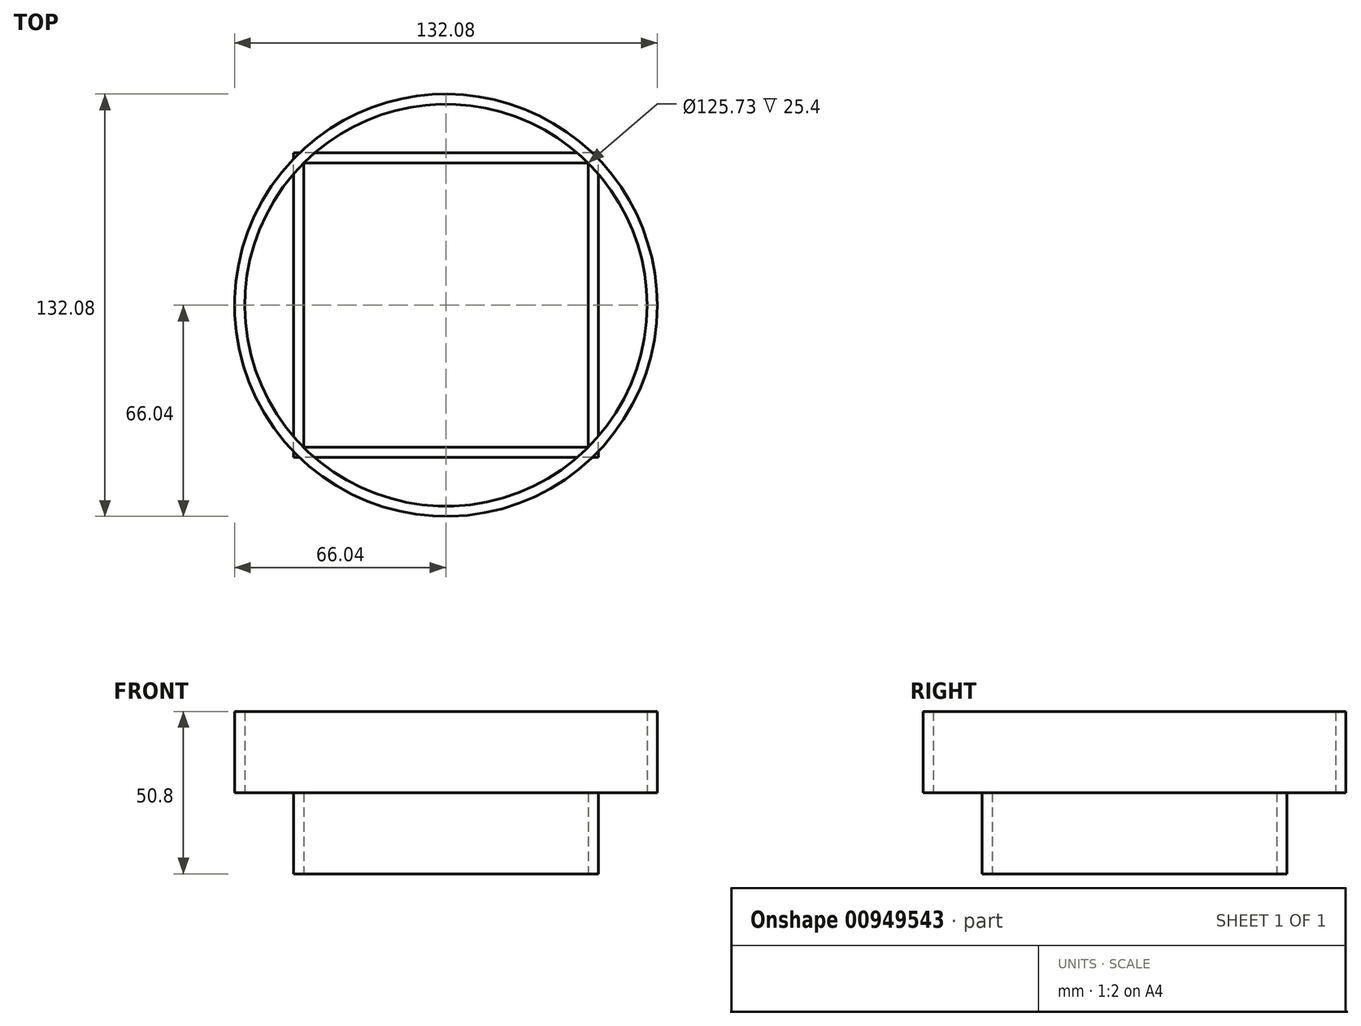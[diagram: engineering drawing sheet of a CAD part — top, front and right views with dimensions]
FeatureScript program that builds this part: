
annotation { "Feature Type Name" : "Feature", "Feature Type Description" : "" }
export const myFeature = defineFeature(function(context is Context, id is Id, definition is map)
    precondition{}
    {
        {
            var Q0;
            Q0=qCreatedBy(makeId("Top.planeOp"),FACE);
            var sketch = newSketch(context, id + "F0", { "sketchPlane" : qUnion([Q0])});
            skLineSegment(sketch, "E0.bottom", {"start": v(44.45, -44.45) * mm, "end": v(-44.45, -44.45) * mm});
            skLineSegment(sketch, "E0.top", {"start": v(44.45, 44.45) * mm, "end": v(-44.45, 44.45) * mm});
            skLineSegment(sketch, "E0.left", {"start": v(44.45, -44.45) * mm, "end": v(44.45, 44.45) * mm});
            skLineSegment(sketch, "E0.right", {"start": v(-44.45, -44.45) * mm, "end": v(-44.45, 44.45) * mm});
            skPoint(sketch, "E0.middle", {"position": v(0, 0) * mm});
            skLineSegment(sketch, "E1.0", {"start": v(47.62, 47.62) * mm, "end": v(-47.62, 47.62) * mm});
            skLineSegment(sketch, "E1.1", {"start": v(47.62, -47.62) * mm, "end": v(47.62, 47.62) * mm});
            skLineSegment(sketch, "E1.2", {"start": v(47.62, -47.62) * mm, "end": v(-47.62, -47.63) * mm});
            skLineSegment(sketch, "E1.3", {"start": v(-47.62, -47.63) * mm, "end": v(-47.62, 47.62) * mm});
            skSolve(sketch);
        }
        {
            var Q0;
            Q0=makeQuery(id+"F0.imprint","IMPRINT",FACE,{"disambiguationData":[TD([[makeQuery(id+"F0.imprint","IMPRINT",EDGE,{"derivedFrom":sQuery(id+"F0.wireOp",EDGE,"E0.bottom")}),1.0]])]});
            extrude(context, id + "F1", {"entities" : qUnion([Q0]), "depth" : 25.4 * mm, "offsetDistance" : 25.4 * mm});
        }
        {
            var Q0;
            Q0=makeQuery(id+"F1.opExtrude","CAP_FACE",FACE,{"disambiguationData":[OSD([sQuery(id+"F0.wireOp",EDGE,"E0.bottom"),sQuery(id+"F0.wireOp",EDGE,"E0.top"),sQuery(id+"F0.wireOp",EDGE,"E0.left"),sQuery(id+"F0.wireOp",EDGE,"E0.right"),sQuery(id+"F0.wireOp",EDGE,"E1.0"),sQuery(id+"F0.wireOp",EDGE,"E1.1"),sQuery(id+"F0.wireOp",EDGE,"E1.2"),sQuery(id+"F0.wireOp",EDGE,"E1.3")])],"isStart":false});
            var sketch = newSketch(context, id + "F2", { "sketchPlane" : qUnion([Q0])});
            skCircle(sketch, "E2", {"center": v(0, 0) * mm, "radius": 66.04 * mm});
            skCircle(sketch, "E3.0", {"center": v(0, 0) * mm, "radius": 62.87 * mm});
            skSolve(sketch);
        }
        {
            var Q0;
            {var subQ0=sQuery(id+"F2.wireOp",EDGE,"E2");var subQ1=makeQuery(id+"F1.opExtrude","CAP_EDGE",EDGE,{"disambiguationData":[OSD([sQuery(id+"F0.wireOp",EDGE,"E1.1")])],"isStart":false});var subQ2=makeQuery(id+"F2.imprint","INTERSECT",VERTEX,{"disambiguationData":[OD(0.0)],"derivedFrom":[subQ1,subQ0]});Q0=makeQuery(id+"F2.imprint","IMPRINT",FACE,{"disambiguationData":[TD([[makeQuery(id+"F2.imprint","IMPRINT",EDGE,{"disambiguationData":[TD([[subQ2,1.0]])],"derivedFrom":subQ0}),1.0]])]});}
            var Q1;
            {var subQ0=sQuery(id+"F2.wireOp",EDGE,"E2");var subQ1=makeQuery(id+"F1.opExtrude","CAP_EDGE",EDGE,{"disambiguationData":[OSD([sQuery(id+"F0.wireOp",EDGE,"E1.0")])],"isStart":false});var subQ2=makeQuery(id+"F2.imprint","INTERSECT",VERTEX,{"disambiguationData":[OD(0.0)],"derivedFrom":[subQ1,subQ0]});Q1=makeQuery(id+"F2.imprint","IMPRINT",FACE,{"disambiguationData":[TD([[makeQuery(id+"F2.imprint","IMPRINT",EDGE,{"disambiguationData":[TD([[subQ2,1.0]])],"derivedFrom":subQ0}),1.0]])]});}
            var Q2;
            {var subQ0=sQuery(id+"F2.wireOp",EDGE,"E2");var subQ1=makeQuery(id+"F1.opExtrude","CAP_EDGE",EDGE,{"disambiguationData":[OSD([sQuery(id+"F0.wireOp",EDGE,"E1.0")])],"isStart":false});var subQ2=makeQuery(id+"F2.imprint","INTERSECT",VERTEX,{"disambiguationData":[OD(0.0)],"derivedFrom":[subQ1,subQ0]});Q2=makeQuery(id+"F2.imprint","IMPRINT",FACE,{"disambiguationData":[TD([[makeQuery(id+"F2.imprint","IMPRINT",EDGE,{"disambiguationData":[TD([[subQ2,-1.0]])],"derivedFrom":subQ0}),1.0]])]});}
            var Q3;
            {var subQ0=sQuery(id+"F2.wireOp",EDGE,"E2");var subQ1=makeQuery(id+"F1.opExtrude","CAP_EDGE",EDGE,{"disambiguationData":[OSD([sQuery(id+"F0.wireOp",EDGE,"E1.2")])],"isStart":false});var subQ2=makeQuery(id+"F2.imprint","INTERSECT",VERTEX,{"disambiguationData":[OD(0.0)],"derivedFrom":[subQ1,subQ0]});Q3=makeQuery(id+"F2.imprint","IMPRINT",FACE,{"disambiguationData":[TD([[makeQuery(id+"F2.imprint","IMPRINT",EDGE,{"disambiguationData":[TD([[subQ2,-1.0]])],"derivedFrom":subQ0}),1.0]])]});}
            var Q4;
            {var subQ0=sQuery(id+"F2.wireOp",EDGE,"E2");var subQ1=makeQuery(id+"F1.opExtrude","CAP_EDGE",EDGE,{"disambiguationData":[OSD([sQuery(id+"F0.wireOp",EDGE,"E1.2")])],"isStart":false});var subQ2=makeQuery(id+"F2.imprint","INTERSECT",VERTEX,{"disambiguationData":[OD(1.0)],"derivedFrom":[subQ1,subQ0]});Q4=makeQuery(id+"F2.imprint","IMPRINT",FACE,{"disambiguationData":[TD([[makeQuery(id+"F2.imprint","IMPRINT",EDGE,{"disambiguationData":[TD([[subQ2,-1.0]])],"derivedFrom":subQ0}),1.0]])]});}
            var Q5;
            {var subQ0=sQuery(id+"F2.wireOp",EDGE,"E2");var subQ1=makeQuery(id+"F1.opExtrude","CAP_EDGE",EDGE,{"disambiguationData":[OSD([sQuery(id+"F0.wireOp",EDGE,"E1.3")])],"isStart":false});var subQ2=makeQuery(id+"F2.imprint","INTERSECT",VERTEX,{"disambiguationData":[OD(0.0)],"derivedFrom":[subQ1,subQ0]});Q5=makeQuery(id+"F2.imprint","IMPRINT",FACE,{"disambiguationData":[TD([[makeQuery(id+"F2.imprint","IMPRINT",EDGE,{"disambiguationData":[TD([[subQ2,-1.0]])],"derivedFrom":subQ0}),1.0]])]});}
            var Q6;
            {var subQ0=sQuery(id+"F2.wireOp",EDGE,"E2");var subQ1=makeQuery(id+"F1.opExtrude","CAP_EDGE",EDGE,{"disambiguationData":[OSD([sQuery(id+"F0.wireOp",EDGE,"E1.3")])],"isStart":false});var subQ2=makeQuery(id+"F2.imprint","INTERSECT",VERTEX,{"disambiguationData":[OD(1.0)],"derivedFrom":[subQ1,subQ0]});Q6=makeQuery(id+"F2.imprint","IMPRINT",FACE,{"disambiguationData":[TD([[makeQuery(id+"F2.imprint","IMPRINT",EDGE,{"disambiguationData":[TD([[subQ2,-1.0]])],"derivedFrom":subQ0}),1.0]])]});}
            var Q7;
            {var subQ0=sQuery(id+"F2.wireOp",EDGE,"E2");var subQ1=makeQuery(id+"F1.opExtrude","CAP_EDGE",EDGE,{"disambiguationData":[OSD([sQuery(id+"F0.wireOp",EDGE,"E1.0")])],"isStart":false});var subQ2=makeQuery(id+"F2.imprint","INTERSECT",VERTEX,{"disambiguationData":[OD(1.0)],"derivedFrom":[subQ1,subQ0]});Q7=makeQuery(id+"F2.imprint","IMPRINT",FACE,{"disambiguationData":[TD([[makeQuery(id+"F2.imprint","IMPRINT",EDGE,{"disambiguationData":[TD([[subQ2,-1.0]])],"derivedFrom":subQ0}),1.0]])]});}
            extrude(context, id + "F3", {"entities" : qUnion([Q0, Q1, Q2, Q3, Q4, Q5, Q6, Q7]), "operationType" : NewBodyOperationType.ADD, "depth" : 25.4 * mm, "offsetDistance" : 25.4 * mm});
        }
    });
